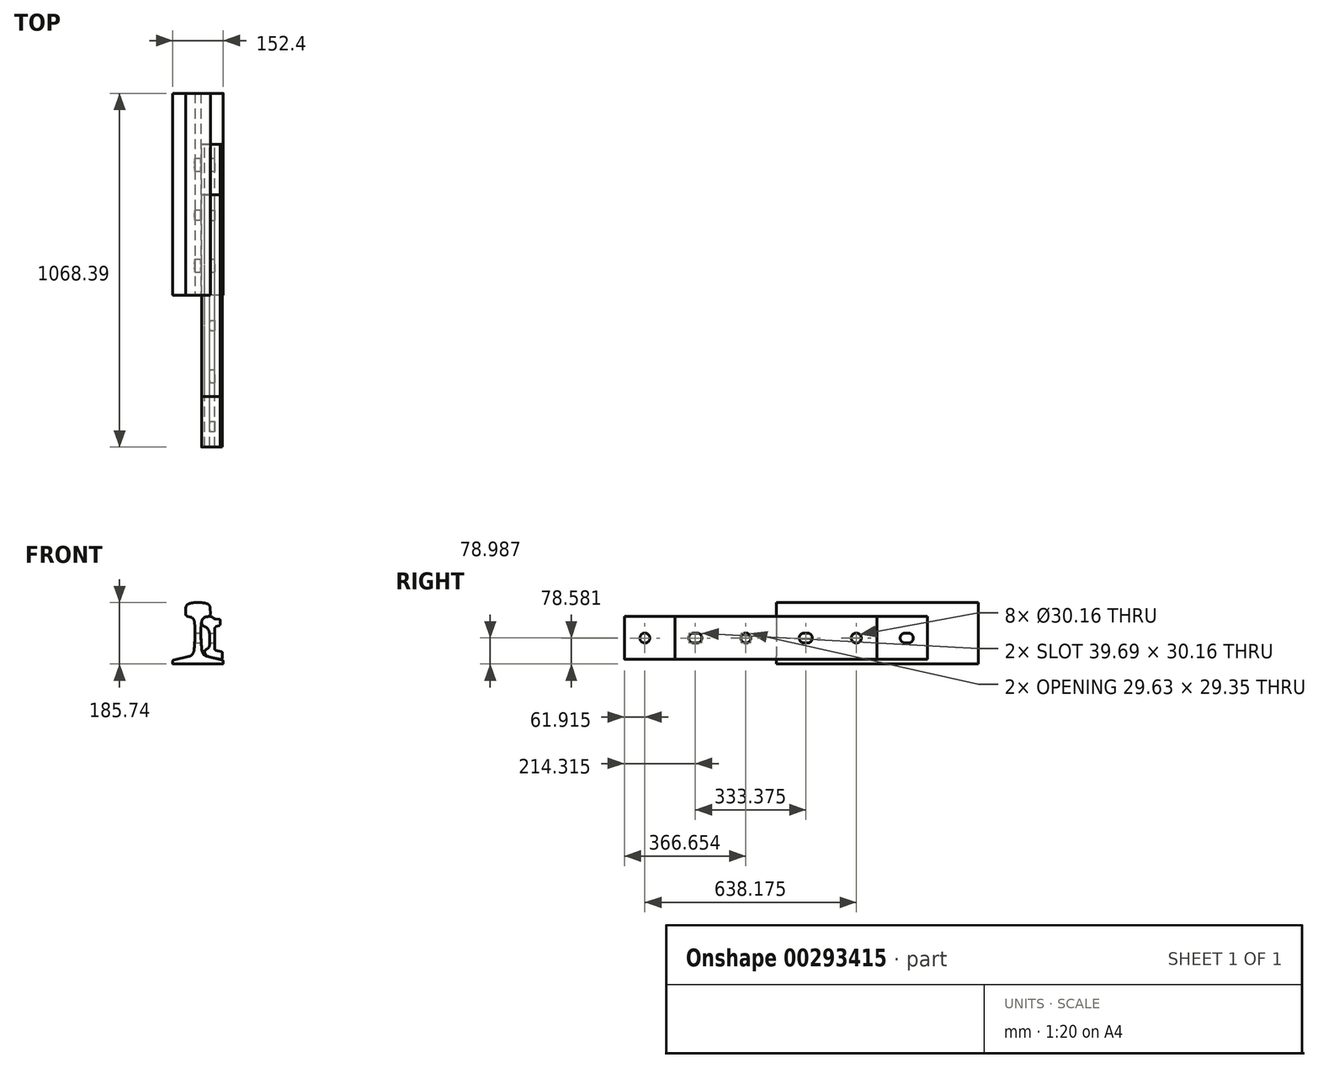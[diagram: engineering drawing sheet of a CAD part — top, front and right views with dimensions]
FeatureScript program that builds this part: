
annotation { "Feature Type Name" : "Feature", "Feature Type Description" : "" }
export const myFeature = defineFeature(function(context is Context, id is Id, definition is map)
    precondition{}
    {
        {
            var Q0;
            Q0=qCreatedBy(makeId("Front.planeOp"),FACE);
            var sketch = newSketch(context, id + "F0", { "sketchPlane" : qUnion([Q0])});
            skLineSegment(sketch, "E0", {"start": v(0, 0) * mm, "end": v(74.61, 0) * mm});
            skArc(sketch, "E1", {"start": v(74.61, 0) * mm, "mid": v(75.74, 0.46) * mm, "end": v(76.2, 1.59) * mm});
            skLineSegment(sketch, "E2", {"start": v(76.2, 1.59) * mm, "end": v(76.2, 8.64) * mm});
            skArc(sketch, "E3", {"start": v(76.2, 8.64) * mm, "mid": v(75.53, 10.6) * mm, "end": v(73.8, 11.72) * mm});
            skLineSegment(sketch, "E4", {"start": v(73.8, 11.72) * mm, "end": v(26.42, 23.56) * mm});
            skArc(sketch, "E5", {"start": v(12.12, 39.84) * mm, "mid": v(16.73, 29.47) * mm, "end": v(26.42, 23.56) * mm});
            skArc(sketch, "E6", {"start": v(8.73, 98.42) * mm, "mid": v(9.58, 69.08) * mm, "end": v(12.12, 39.84) * mm});
            skArc(sketch, "E7", {"start": v(10.86, 127.8) * mm, "mid": v(9.27, 113.15) * mm, "end": v(8.73, 98.43) * mm});
            skArc(sketch, "E8", {"start": v(18.92, 140.74) * mm, "mid": v(13.54, 135.1) * mm, "end": v(10.86, 127.8) * mm});
            skLineSegment(sketch, "E9", {"start": v(21.5, 141.9) * mm, "end": v(31.96, 144.51) * mm});
            skArc(sketch, "E10", {"start": v(31.96, 144.51) * mm, "mid": v(35.87, 147.09) * mm, "end": v(37.3, 151.54) * mm});
            skLineSegment(sketch, "E11", {"start": v(37.3, 151.54) * mm, "end": v(36.86, 169.37) * mm});
            skArc(sketch, "E12", {"start": v(36.86, 169.37) * mm, "mid": v(35.54, 175.02) * mm, "end": v(32.08, 179.68) * mm});
            skArc(sketch, "E13.MirrorCS", {"start": v(-74.61, 0) * mm, "mid": v(-75.74, 0.46) * mm, "end": v(-76.2, 1.59) * mm});
            skArc(sketch, "E14.MirrorCS", {"start": v(-31.96, 144.51) * mm, "mid": v(-35.87, 147.09) * mm, "end": v(-37.3, 151.54) * mm});
            skArc(sketch, "E15.MirrorCS", {"start": v(-76.2, 8.64) * mm, "mid": v(-75.53, 10.6) * mm, "end": v(-73.8, 11.72) * mm});
            skLineSegment(sketch, "E16.MirrorCS", {"start": v(-21.5, 141.9) * mm, "end": v(-31.96, 144.51) * mm});
            skLineSegment(sketch, "E17.MirrorCS", {"start": v(-76.2, 1.59) * mm, "end": v(-76.2, 8.64) * mm});
            skArc(sketch, "E18.MirrorCS", {"start": v(-36.86, 169.37) * mm, "mid": v(-35.54, 175.02) * mm, "end": v(-32.08, 179.68) * mm});
            skLineSegment(sketch, "E19.MirrorCS", {"start": v(-37.3, 151.54) * mm, "end": v(-36.86, 169.37) * mm});
            skLineSegment(sketch, "E20.MirrorCS", {"start": v(-73.8, 11.72) * mm, "end": v(-26.42, 23.56) * mm});
            skLineSegment(sketch, "E21.MirrorCS", {"start": v(0, 0) * mm, "end": v(-74.61, 0) * mm});
            skArc(sketch, "E22.MirrorCS", {"start": v(-10.86, 127.8) * mm, "mid": v(-9.27, 113.15) * mm, "end": v(-8.73, 98.43) * mm});
            skArc(sketch, "E23.MirrorCS", {"start": v(-8.73, 98.42) * mm, "mid": v(-9.58, 69.08) * mm, "end": v(-12.12, 39.84) * mm});
            skArc(sketch, "E24.MirrorCS", {"start": v(-12.12, 39.84) * mm, "mid": v(-16.73, 29.47) * mm, "end": v(-26.42, 23.56) * mm});
            skArc(sketch, "E25.MirrorCS", {"start": v(-18.92, 140.74) * mm, "mid": v(-13.54, 135.1) * mm, "end": v(-10.86, 127.8) * mm});
            skPoint(sketch, "E26", {"position": v(0, 30.16) * mm});
            skLineSegment(sketch, "E27", {"start": v(0, 30.16) * mm, "end": v(-73.03, 30.16) * mm, "construction": true});
            skLineSegment(sketch, "E28", {"start": v(0, 30.16) * mm, "end": v(-73.8, 11.72) * mm, "construction": true});
            skPoint(sketch, "E29", {"position": v(0, 136.53) * mm});
            skLineSegment(sketch, "E30", {"start": v(0, 136.53) * mm, "end": v(-69.8, 136.53) * mm, "construction": true});
            skLineSegment(sketch, "E31", {"start": v(0, 136.52) * mm, "end": v(-67.13, 153.3) * mm, "construction": true});
            skArc(sketch, "E32", {"start": v(14.09, 185.25) * mm, "mid": v(7.05, 185.62) * mm, "end": v(0, 185.74) * mm});
            skArc(sketch, "E33", {"start": v(29.77, 181.2) * mm, "mid": v(22.11, 183.95) * mm, "end": v(14.09, 185.25) * mm});
            skArc(sketch, "E34.MirrorCS", {"start": v(-29.77, 181.2) * mm, "mid": v(-22.11, 183.95) * mm, "end": v(-14.09, 185.25) * mm});
            skArc(sketch, "E35.MirrorCS", {"start": v(-14.09, 185.25) * mm, "mid": v(-7.05, 185.62) * mm, "end": v(0, 185.74) * mm});
            skArc(sketch, "E36", {"start": v(32.08, 179.68) * mm, "mid": v(30.98, 180.53) * mm, "end": v(29.77, 181.2) * mm});
            skArc(sketch, "E37.MirrorCS", {"start": v(-32.08, 179.68) * mm, "mid": v(-30.98, 180.53) * mm, "end": v(-29.77, 181.2) * mm});
            skArc(sketch, "E38", {"start": v(21.5, 141.9) * mm, "mid": v(20.15, 141.43) * mm, "end": v(18.92, 140.74) * mm});
            skArc(sketch, "E39.MirrorCS", {"start": v(-21.5, 141.9) * mm, "mid": v(-20.15, 141.43) * mm, "end": v(-18.92, 140.74) * mm});
            skLineSegment(sketch, "E40", {"start": v(-37.3, 151.54) * mm, "end": v(-37.3, 178.33) * mm, "construction": true});
            skPoint(sketch, "E41", {"position": v(0, 129.38) * mm});
            skLineSegment(sketch, "E42", {"start": v(211.93, 98.42) * mm, "end": v(0, 129.38) * mm, "construction": true});
            skSolve(sketch);
        }
        {
            var Q0;
            Q0=makeQuery(id+"F0.imprint","IMPRINT",FACE,{"disambiguationData":[TD([[makeQuery(id+"F0.imprint","IMPRINT",EDGE,{"derivedFrom":sQuery(id+"F0.wireOp",EDGE,"E0")}),1.0]])]});
            extrude(context, id + "F1", {"entities" : qUnion([Q0]), "oppositeDirection" : true, "depth" : 609.6 * mm});
        }
        {
            var Q0;
            Q0=qCreatedBy(makeId("Right.planeOp"),FACE);
            cPlane(context, id + "F2", {"entities" : qUnion([Q0]), "cplaneType" : CPlaneType.OFFSET, "offset" : 76.2 * mm, "width" : 152.4 * mm, "height" : 152.4 * mm});
        }
        {
            var Q0;
            Q0=qCreatedBy(id+"F2.planeOp",FACE);
            var sketch = newSketch(context, id + "F3", { "sketchPlane" : qUnion([Q0])});
            skPoint(sketch, "E43", {"position": v(88.9, 78.58) * mm});
            skPoint(sketch, "E44", {"position": v(241.3, 78.58) * mm});
            skPoint(sketch, "E45", {"position": v(393.7, 78.58) * mm});
            skLineSegment(sketch, "E46", {"start": v(-1.59, 197.18) * mm, "end": v(-1.59, -40.46) * mm, "construction": true});
            skPoint(sketch, "E47.MirrorP", {"position": v(-396.88, 78.58) * mm});
            skPoint(sketch, "E48.MirrorP", {"position": v(-244.48, 78.58) * mm});
            skPoint(sketch, "E49.MirrorP", {"position": v(-92.08, 78.58) * mm});
            skCircle(sketch, "E50", {"center": v(-396.88, 78.58) * mm, "radius": 15.08 * mm});
            skCircle(sketch, "E51", {"center": v(-92.08, 78.58) * mm, "radius": 15.08 * mm});
            skCircle(sketch, "E52", {"center": v(241.3, 78.58) * mm, "radius": 15.08 * mm});
            skLineSegment(sketch, "E53", {"start": v(-249.24, 78.58) * mm, "end": v(-239.71, 78.58) * mm, "construction": true});
            skArc(sketch, "E54", {"start": v(-249.24, 93.66) * mm, "mid": v(-264.32, 78.58) * mm, "end": v(-249.24, 63.5) * mm});
            skArc(sketch, "E55", {"start": v(-239.71, 93.66) * mm, "mid": v(-224.63, 78.58) * mm, "end": v(-239.71, 63.5) * mm});
            skLineSegment(sketch, "E56", {"start": v(-249.24, 93.66) * mm, "end": v(-239.71, 93.66) * mm});
            skLineSegment(sketch, "E57", {"start": v(-249.24, 63.5) * mm, "end": v(-239.71, 63.5) * mm});
            skLineSegment(sketch, "E58", {"start": v(84.14, 78.58) * mm, "end": v(93.66, 78.58) * mm, "construction": true});
            skArc(sketch, "E59", {"start": v(84.14, 93.66) * mm, "mid": v(69.06, 78.58) * mm, "end": v(84.14, 63.5) * mm});
            skArc(sketch, "E60", {"start": v(93.66, 93.66) * mm, "mid": v(108.74, 78.58) * mm, "end": v(93.66, 63.5) * mm});
            skLineSegment(sketch, "E61", {"start": v(84.14, 93.66) * mm, "end": v(93.66, 93.66) * mm});
            skLineSegment(sketch, "E62", {"start": v(84.14, 63.5) * mm, "end": v(93.66, 63.5) * mm});
            skLineSegment(sketch, "E63", {"start": v(388.94, 78.58) * mm, "end": v(398.46, 78.58) * mm, "construction": true});
            skArc(sketch, "E64", {"start": v(388.94, 93.66) * mm, "mid": v(373.86, 78.58) * mm, "end": v(388.94, 63.5) * mm});
            skArc(sketch, "E65", {"start": v(398.46, 93.66) * mm, "mid": v(413.54, 78.58) * mm, "end": v(398.46, 63.5) * mm});
            skLineSegment(sketch, "E66", {"start": v(388.94, 93.66) * mm, "end": v(398.46, 93.66) * mm});
            skLineSegment(sketch, "E67", {"start": v(388.94, 63.5) * mm, "end": v(398.46, 63.5) * mm});
            skSolve(sketch);
        }
        {
            var Q0;
            Q0=makeQuery(id+"F0.imprint","IMPRINT",FACE,{"disambiguationData":[TD([[makeQuery(id+"F0.imprint","IMPRINT",EDGE,{"derivedFrom":sQuery(id+"F0.wireOp",EDGE,"E0")}),1.0]])]});
            extrude(context, id + "F4", {"entities" : qUnion([Q0]), "oppositeDirection" : true, "depth" : 609.6 * mm});
        }
        {
            var Q0;
            Q0=sQuery(id+"F3.wireOp",VERTEX,"E43");
            var Q1;
            Q1=sQuery(id+"F3.wireOp",VERTEX,"E44");
            var Q2;
            Q2=makeQuery(id+"F4.opExtrude","SWEPT_BODY",BODY,{"disambiguationData":[OSD([sQuery(id+"F0.wireOp",EDGE,"E0"),sQuery(id+"F0.wireOp",EDGE,"E1"),sQuery(id+"F0.wireOp",EDGE,"E2"),sQuery(id+"F0.wireOp",EDGE,"E3"),sQuery(id+"F0.wireOp",EDGE,"E4"),sQuery(id+"F0.wireOp",EDGE,"E5"),sQuery(id+"F0.wireOp",EDGE,"E6"),sQuery(id+"F0.wireOp",EDGE,"E7"),sQuery(id+"F0.wireOp",EDGE,"E8"),sQuery(id+"F0.wireOp",EDGE,"E9"),sQuery(id+"F0.wireOp",EDGE,"E10"),sQuery(id+"F0.wireOp",EDGE,"E11"),sQuery(id+"F0.wireOp",EDGE,"E12"),sQuery(id+"F0.wireOp",EDGE,"E13.MirrorCS"),sQuery(id+"F0.wireOp",EDGE,"E14.MirrorCS"),sQuery(id+"F0.wireOp",EDGE,"E15.MirrorCS"),sQuery(id+"F0.wireOp",EDGE,"E16.MirrorCS"),sQuery(id+"F0.wireOp",EDGE,"E17.MirrorCS"),sQuery(id+"F0.wireOp",EDGE,"E18.MirrorCS"),sQuery(id+"F0.wireOp",EDGE,"E19.MirrorCS"),sQuery(id+"F0.wireOp",EDGE,"E20.MirrorCS"),sQuery(id+"F0.wireOp",EDGE,"E21.MirrorCS"),sQuery(id+"F0.wireOp",EDGE,"E22.MirrorCS"),sQuery(id+"F0.wireOp",EDGE,"E23.MirrorCS"),sQuery(id+"F0.wireOp",EDGE,"E24.MirrorCS"),sQuery(id+"F0.wireOp",EDGE,"E25.MirrorCS"),sQuery(id+"F0.wireOp",EDGE,"E32"),sQuery(id+"F0.wireOp",EDGE,"E33"),sQuery(id+"F0.wireOp",EDGE,"E34.MirrorCS"),sQuery(id+"F0.wireOp",EDGE,"E35.MirrorCS"),sQuery(id+"F0.wireOp",EDGE,"E36"),sQuery(id+"F0.wireOp",EDGE,"E37.MirrorCS"),sQuery(id+"F0.wireOp",EDGE,"E38"),sQuery(id+"F0.wireOp",EDGE,"E39.MirrorCS")])]});
            hole(context, id + "F5", {"style" : HoleStyle.SIMPLE, "endStyle" : HoleEndStyle.THROUGH, "holeDiameter" : 30.16 * mm, "startFromSketch" : true, "locations" : qUnion([Q0, Q1]), "scope" : qUnion([Q2]), "isTappedThrough" : true});
        }
        {
            var Q0;
            Q0=makeQuery(id+"F0.imprint","IMPRINT",FACE,{"disambiguationData":[TD([[makeQuery(id+"F0.imprint","IMPRINT",EDGE,{"derivedFrom":sQuery(id+"F0.wireOp",EDGE,"E0")}),1.0]])]});
            extrude(context, id + "F6", {"entities" : qUnion([Q0]), "oppositeDirection" : true, "depth" : 609.6 * mm});
        }
        {
            var Q0;
            Q0=sQuery(id+"F3.wireOp",VERTEX,"E43");
            var Q1;
            Q1=sQuery(id+"F3.wireOp",VERTEX,"E44");
            var Q2;
            Q2=sQuery(id+"F3.wireOp",VERTEX,"E45");
            var Q3;
            Q3=makeQuery(id+"F6.opExtrude","SWEPT_BODY",BODY,{"disambiguationData":[OSD([sQuery(id+"F0.wireOp",EDGE,"E0"),sQuery(id+"F0.wireOp",EDGE,"E1"),sQuery(id+"F0.wireOp",EDGE,"E2"),sQuery(id+"F0.wireOp",EDGE,"E3"),sQuery(id+"F0.wireOp",EDGE,"E4"),sQuery(id+"F0.wireOp",EDGE,"E5"),sQuery(id+"F0.wireOp",EDGE,"E6"),sQuery(id+"F0.wireOp",EDGE,"E7"),sQuery(id+"F0.wireOp",EDGE,"E8"),sQuery(id+"F0.wireOp",EDGE,"E9"),sQuery(id+"F0.wireOp",EDGE,"E10"),sQuery(id+"F0.wireOp",EDGE,"E11"),sQuery(id+"F0.wireOp",EDGE,"E12"),sQuery(id+"F0.wireOp",EDGE,"E13.MirrorCS"),sQuery(id+"F0.wireOp",EDGE,"E14.MirrorCS"),sQuery(id+"F0.wireOp",EDGE,"E15.MirrorCS"),sQuery(id+"F0.wireOp",EDGE,"E16.MirrorCS"),sQuery(id+"F0.wireOp",EDGE,"E17.MirrorCS"),sQuery(id+"F0.wireOp",EDGE,"E18.MirrorCS"),sQuery(id+"F0.wireOp",EDGE,"E19.MirrorCS"),sQuery(id+"F0.wireOp",EDGE,"E20.MirrorCS"),sQuery(id+"F0.wireOp",EDGE,"E21.MirrorCS"),sQuery(id+"F0.wireOp",EDGE,"E22.MirrorCS"),sQuery(id+"F0.wireOp",EDGE,"E23.MirrorCS"),sQuery(id+"F0.wireOp",EDGE,"E24.MirrorCS"),sQuery(id+"F0.wireOp",EDGE,"E25.MirrorCS"),sQuery(id+"F0.wireOp",EDGE,"E32"),sQuery(id+"F0.wireOp",EDGE,"E33"),sQuery(id+"F0.wireOp",EDGE,"E34.MirrorCS"),sQuery(id+"F0.wireOp",EDGE,"E35.MirrorCS"),sQuery(id+"F0.wireOp",EDGE,"E36"),sQuery(id+"F0.wireOp",EDGE,"E37.MirrorCS"),sQuery(id+"F0.wireOp",EDGE,"E38"),sQuery(id+"F0.wireOp",EDGE,"E39.MirrorCS")])]});
            hole(context, id + "F7", {"style" : HoleStyle.SIMPLE, "endStyle" : HoleEndStyle.THROUGH, "holeDiameter" : 30.16 * mm, "startFromSketch" : true, "locations" : qUnion([Q0, Q1, Q2]), "scope" : qUnion([Q3]), "isTappedThrough" : true});
        }
        {
            var Q0;
            Q0=qCreatedBy(makeId("Front.planeOp"),FACE);
            cPlane(context, id + "F8", {"entities" : qUnion([Q0]), "cplaneType" : CPlaneType.OFFSET, "offset" : 1.59 * mm, "width" : 152.4 * mm, "height" : 152.4 * mm});
        }
        {
            var Q0;
            Q0=qCreatedBy(id+"F8.planeOp",FACE);
            var sketch = newSketch(context, id + "F9", { "sketchPlane" : qUnion([Q0])});
            skLineSegment(sketch, "E68", {"start": v(72.86, 18.3) * mm, "end": v(72.86, 34.8) * mm});
            skArc(sketch, "E69", {"start": v(72.86, 34.8) * mm, "mid": v(72.34, 36.3) * mm, "end": v(71, 37.15) * mm});
            skLineSegment(sketch, "E70", {"start": v(71, 37.15) * mm, "end": v(54.47, 41.13) * mm});
            skArc(sketch, "E71", {"start": v(50.8, 45.79) * mm, "mid": v(51.83, 42.82) * mm, "end": v(54.47, 41.13) * mm});
            skLineSegment(sketch, "E72", {"start": v(50.8, 45.79) * mm, "end": v(50.8, 107.48) * mm});
            skArc(sketch, "E73", {"start": v(54.7, 113.06) * mm, "mid": v(51.87, 110.88) * mm, "end": v(50.8, 107.48) * mm});
            skLineSegment(sketch, "E74", {"start": v(54.7, 113.06) * mm, "end": v(64.39, 116.62) * mm});
            skArc(sketch, "E75", {"start": v(64.39, 116.62) * mm, "mid": v(66.02, 117.88) * mm, "end": v(66.64, 119.85) * mm});
            skLineSegment(sketch, "E76", {"start": v(66.64, 119.85) * mm, "end": v(66.64, 131.96) * mm});
            skArc(sketch, "E77", {"start": v(66.64, 131.96) * mm, "mid": v(65.7, 134.34) * mm, "end": v(63.37, 135.41) * mm});
            skLineSegment(sketch, "E78", {"start": v(63.37, 135.41) * mm, "end": v(53.1, 135.97) * mm});
            skArc(sketch, "E79", {"start": v(46.54, 139.2) * mm, "mid": v(49.5, 136.91) * mm, "end": v(53.1, 135.97) * mm});
            skArc(sketch, "E80", {"start": v(46.54, 139.2) * mm, "mid": v(41.22, 142.9) * mm, "end": v(34.76, 143.56) * mm});
            skLineSegment(sketch, "E81", {"start": v(34.76, 143.56) * mm, "end": v(28.5, 142.6) * mm});
            skArc(sketch, "E82", {"start": v(24.43, 142.38) * mm, "mid": v(26.48, 142.38) * mm, "end": v(28.5, 142.6) * mm});
            skArc(sketch, "E83", {"start": v(24.43, 142.38) * mm, "mid": v(21.88, 142) * mm, "end": v(19.68, 140.63) * mm});
            skArc(sketch, "E84", {"start": v(11.7, 130.6) * mm, "mid": v(11.73, 121.14) * mm, "end": v(18.52, 114.54) * mm});
            skArc(sketch, "E85", {"start": v(34.92, 90.5) * mm, "mid": v(30.43, 105.05) * mm, "end": v(18.52, 114.54) * mm});
            skLineSegment(sketch, "E86", {"start": v(34.92, 90.5) * mm, "end": v(34.93, 58.13) * mm});
            skArc(sketch, "E87", {"start": v(25.7, 44.86) * mm, "mid": v(32.4, 50.05) * mm, "end": v(34.93, 58.13) * mm});
            skArc(sketch, "E88", {"start": v(25.7, 44.86) * mm, "mid": v(22.25, 42.37) * mm, "end": v(20.61, 38.44) * mm});
            skArc(sketch, "E89", {"start": v(69.02, 14.97) * mm, "mid": v(71.7, 15.76) * mm, "end": v(72.86, 18.3) * mm});
            skLineSegment(sketch, "E90", {"start": v(55.06, 16.94) * mm, "end": v(69.02, 14.97) * mm});
            skArc(sketch, "E91", {"start": v(20.61, 38.44) * mm, "mid": v(22.54, 29.37) * mm, "end": v(29.67, 23.44) * mm});
            skArc(sketch, "E92", {"start": v(29.67, 23.44) * mm, "mid": v(42.18, 19.49) * mm, "end": v(55.06, 16.94) * mm});
            skArc(sketch, "E93", {"start": v(13.36, 133.88) * mm, "mid": v(12.46, 132.27) * mm, "end": v(11.7, 130.6) * mm});
            skArc(sketch, "E94", {"start": v(19.47, 140.46) * mm, "mid": v(19.58, 140.54) * mm, "end": v(19.68, 140.63) * mm});
            skArc(sketch, "E95", {"start": v(19.47, 140.46) * mm, "mid": v(16.08, 137.48) * mm, "end": v(13.36, 133.88) * mm});
            skSolve(sketch);
        }
        {
            var Q0;
            Q0=makeQuery(id+"F9.imprint","IMPRINT",FACE,{"disambiguationData":[TD([[makeQuery(id+"F9.imprint","IMPRINT",EDGE,{"derivedFrom":sQuery(id+"F9.wireOp",EDGE,"E68")}),1.0]])]});
            extrude(context, id + "F10", {"entities" : qUnion([Q0]), "depth" : 609.6 * mm, "symmetric" : true});
        }
        {
            var Q0;
            Q0=makeQuery(id+"F3.imprint","IMPRINT",FACE,{"disambiguationData":[TD([[makeQuery(id+"F3.imprint","IMPRINT",EDGE,{"derivedFrom":sQuery(id+"F3.wireOp",EDGE,"E54")}),1.0]])]});
            var Q1;
            Q1=makeQuery(id+"F3.imprint","IMPRINT",FACE,{"disambiguationData":[TD([[makeQuery(id+"F3.imprint","IMPRINT",EDGE,{"derivedFrom":sQuery(id+"F3.wireOp",EDGE,"E51")}),1.0]])]});
            var Q2;
            Q2=makeQuery(id+"F3.imprint","IMPRINT",FACE,{"disambiguationData":[TD([[makeQuery(id+"F3.imprint","IMPRINT",EDGE,{"derivedFrom":sQuery(id+"F3.wireOp",EDGE,"E59")}),1.0]])]});
            var Q3;
            Q3=makeQuery(id+"F3.imprint","IMPRINT",FACE,{"disambiguationData":[TD([[makeQuery(id+"F3.imprint","IMPRINT",EDGE,{"derivedFrom":sQuery(id+"F3.wireOp",EDGE,"E52")}),1.0]])]});
            extrude(context, id + "F11", {"entities" : qUnion([Q0, Q1, Q2, Q3]), "operationType" : NewBodyOperationType.REMOVE, "endBound" : BoundingType.THROUGH_ALL, "oppositeDirection" : true, "depth" : 25.4 * mm});
        }
        {
            var Q0;
            Q0=makeQuery(id+"F9.imprint","IMPRINT",FACE,{"disambiguationData":[TD([[makeQuery(id+"F9.imprint","IMPRINT",EDGE,{"derivedFrom":sQuery(id+"F9.wireOp",EDGE,"E68")}),1.0]])]});
            extrude(context, id + "F12", {"entities" : qUnion([Q0]), "depth" : 914.4 * mm, "symmetric" : true});
        }
        {
            var Q0;
            Q0=makeQuery(id+"F3.imprint","IMPRINT",FACE,{"disambiguationData":[TD([[makeQuery(id+"F3.imprint","IMPRINT",EDGE,{"derivedFrom":sQuery(id+"F3.wireOp",EDGE,"E50")}),1.0]])]});
            var Q1;
            Q1=makeQuery(id+"F3.imprint","IMPRINT",FACE,{"disambiguationData":[TD([[makeQuery(id+"F3.imprint","IMPRINT",EDGE,{"derivedFrom":sQuery(id+"F3.wireOp",EDGE,"E54")}),1.0]])]});
            var Q2;
            Q2=makeQuery(id+"F3.imprint","IMPRINT",FACE,{"disambiguationData":[TD([[makeQuery(id+"F3.imprint","IMPRINT",EDGE,{"derivedFrom":sQuery(id+"F3.wireOp",EDGE,"E51")}),1.0]])]});
            var Q3;
            Q3=makeQuery(id+"F3.imprint","IMPRINT",FACE,{"disambiguationData":[TD([[makeQuery(id+"F3.imprint","IMPRINT",EDGE,{"derivedFrom":sQuery(id+"F3.wireOp",EDGE,"E59")}),1.0]])]});
            var Q4;
            Q4=makeQuery(id+"F3.imprint","IMPRINT",FACE,{"disambiguationData":[TD([[makeQuery(id+"F3.imprint","IMPRINT",EDGE,{"derivedFrom":sQuery(id+"F3.wireOp",EDGE,"E52")}),1.0]])]});
            var Q5;
            Q5=makeQuery(id+"F3.imprint","IMPRINT",FACE,{"disambiguationData":[TD([[makeQuery(id+"F3.imprint","IMPRINT",EDGE,{"derivedFrom":sQuery(id+"F3.wireOp",EDGE,"E64")}),1.0]])]});
            extrude(context, id + "F13", {"entities" : qUnion([Q0, Q1, Q2, Q3, Q4, Q5]), "operationType" : NewBodyOperationType.REMOVE, "endBound" : BoundingType.THROUGH_ALL, "oppositeDirection" : true, "depth" : 25.4 * mm});
        }
    });
